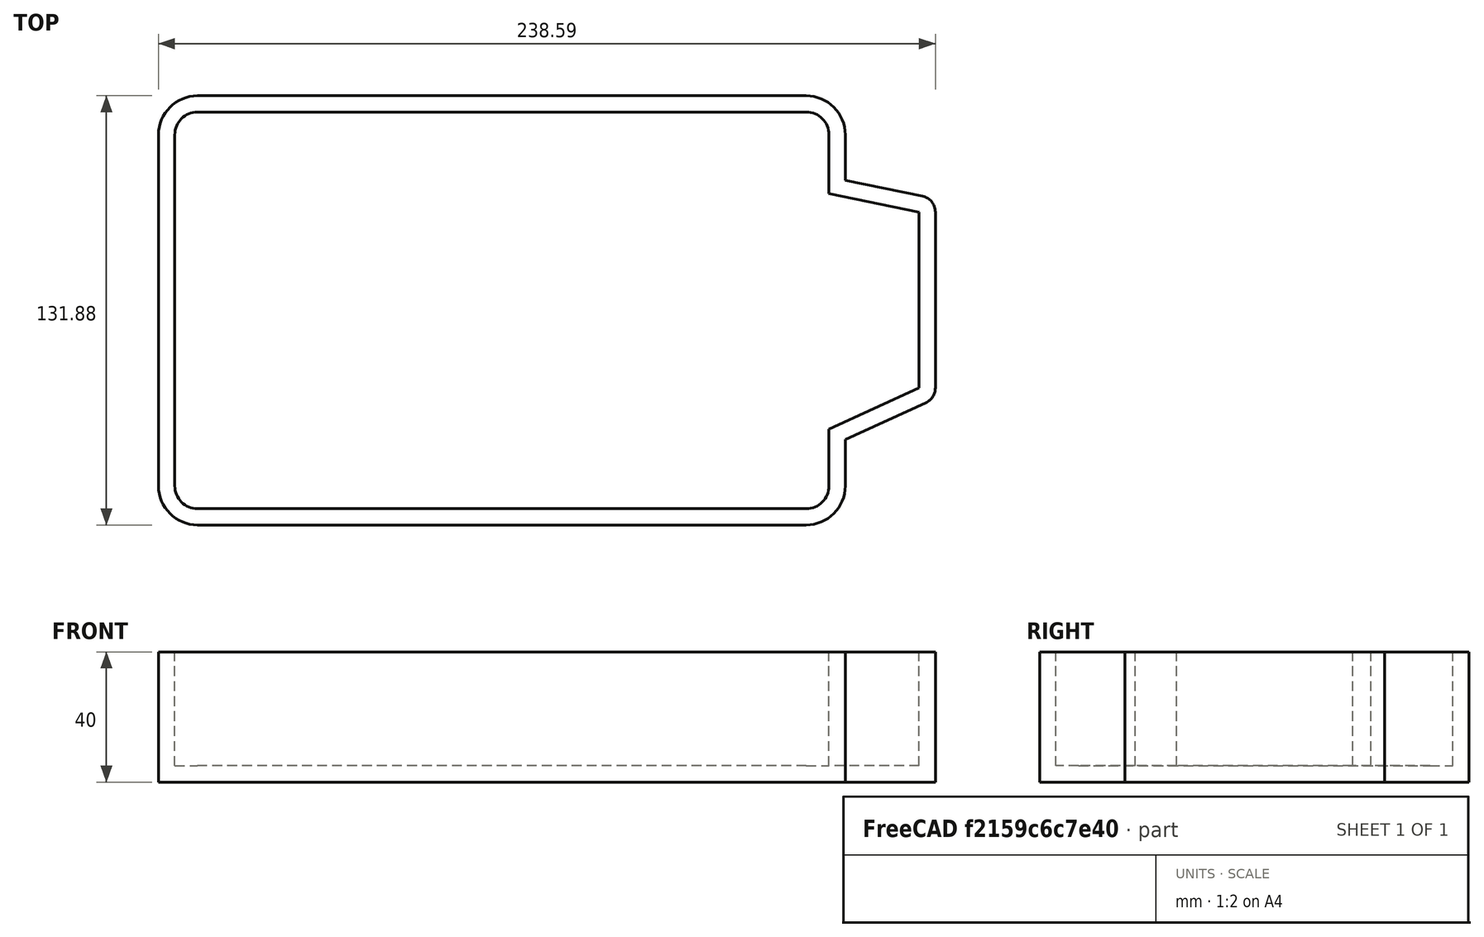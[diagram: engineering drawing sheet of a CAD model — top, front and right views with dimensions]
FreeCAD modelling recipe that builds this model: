
FCSTD DOCUMENT  (FreeCAD 0.19R24366 (Git))
Label: box
License: All rights reserved
LicenseURL: http://en.wikipedia.org/wiki/All_rights_reserved
objects: Part::Extrusion×2, Sketcher::SketchObject×1, Part::Offset2D×1, Part::Cut×1
note: 5 computed .brp shape members not serialized (recipe doc carries the construction recipe); baked Part::Feature solids carry a one-line shape summary decoded from their .brp

FEATURE [Sketcher::SketchObject] Sketch
  FullyConstrained = false
  sketch-geometry (12):
    g0: LineSegment StartX=-92.9294 StartY=60.0812 StartZ=0 EndX=93.9985 EndY=60.0812 EndZ=0
    g1: LineSegment StartX=100.998 StartY=53.0812 StartZ=0 EndX=100.998 EndY=35.0482 EndZ=0
    g2: LineSegment StartX=93.9985 StartY=-61.8039 StartZ=0 EndX=-92.9294 EndY=-61.8039 EndZ=0
    g3: LineSegment StartX=-99.9294 StartY=-54.8039 StartZ=0 EndX=-99.9294 EndY=53.0812 EndZ=0
    g4: LineSegment StartX=100.998 StartY=35.0482 StartZ=0 EndX=128.658 EndY=29.3351 EndZ=0
    g5: LineSegment StartX=128.658 StartY=29.3351 StartZ=0 EndX=128.658 EndY=-24.6804 EndZ=0
    g6: LineSegment StartX=128.658 StartY=-24.6804 StartZ=0 EndX=100.998 EndY=-37.4052 EndZ=0
    g7: LineSegment StartX=100.998 StartY=-37.4052 StartZ=0 EndX=100.998 EndY=-54.8039 EndZ=0
    g8: ArcOfCircle CenterX=-92.9294 CenterY=53.0812 CenterZ=0 NormalX=0 NormalY=0 NormalZ=1 AngleXU=0 Radius=7 StartAngle=1.5708 EndAngle=3.14159
    g9: ArcOfCircle CenterX=-92.9294 CenterY=-54.8039 CenterZ=0 NormalX=0 NormalY=0 NormalZ=1 AngleXU=0 Radius=7 StartAngle=3.14159 EndAngle=4.71239
    g10: ArcOfCircle CenterX=93.9985 CenterY=53.0812 CenterZ=0 NormalX=0 NormalY=0 NormalZ=1 AngleXU=0 Radius=7 StartAngle=0 EndAngle=1.5708
    g11: ArcOfCircle CenterX=93.9985 CenterY=-54.8039 CenterZ=0 NormalX=0 NormalY=0 NormalZ=1 AngleXU=0 Radius=7 StartAngle=4.71239 EndAngle=6.28319
  constraints (22):
    c: Horizontal(g0)
    c: Horizontal(g2)
    c: Vertical(g1)
    c: Vertical(g3)
    c: Coincident(g4,g5)
    c: Vertical(g5)
    c: Coincident(g5,g6)
    c: Coincident(g1,g4)
    c: Coincident(g7,g6)
    c: Tangent(g1,g7)
    c: Tangent(g3,g8) = 1.5708
    c: Tangent(g0,g8) = 1.5708
    c: Tangent(g2,g9) = 1.5708
    c: Tangent(g3,g9) = 1.5708
    c: Tangent(g0,g10) = 1.5708
    c: Tangent(g1,g10) = 1.5708
    c: Tangent(g7,g11) = 1.5708
    c: Tangent(g2,g11) = 1.5708
    c: Equal(g8,g9)
    c: Equal(g8,g11)
    c: Equal(g8,g10)
    c: Radius(g8) = 7
FEATURE [Part::Offset2D] Offset2D
  Fill = false
  Intersection = false
  Join = 0
  Mode = 1
  SelfIntersection = false
  Source = -> Sketch
  Value = 5
FEATURE [Part::Extrusion] Extrude
  Base = -> Sketch
  Dir = (0,0,1)
  DirMode = 2
  FaceMakerClass = Part::FaceMakerBullseye
  LengthFwd = 40
  LengthRev = 0
  Placement = pos=(0,0,5) rot=(0,0,1;0rad)
  Solid = true
  Symmetric = false
FEATURE [Part::Extrusion] Extrude001
  Base = -> Offset2D
  Dir = (0,0,1)
  DirMode = 2
  FaceMakerClass = Part::FaceMakerBullseye
  LengthFwd = 40
  LengthRev = 0
  Solid = true
  Symmetric = false
FEATURE [Part::Cut] Cut  label="Bottom"
  Base = -> Extrude001
  Tool = -> Extrude
